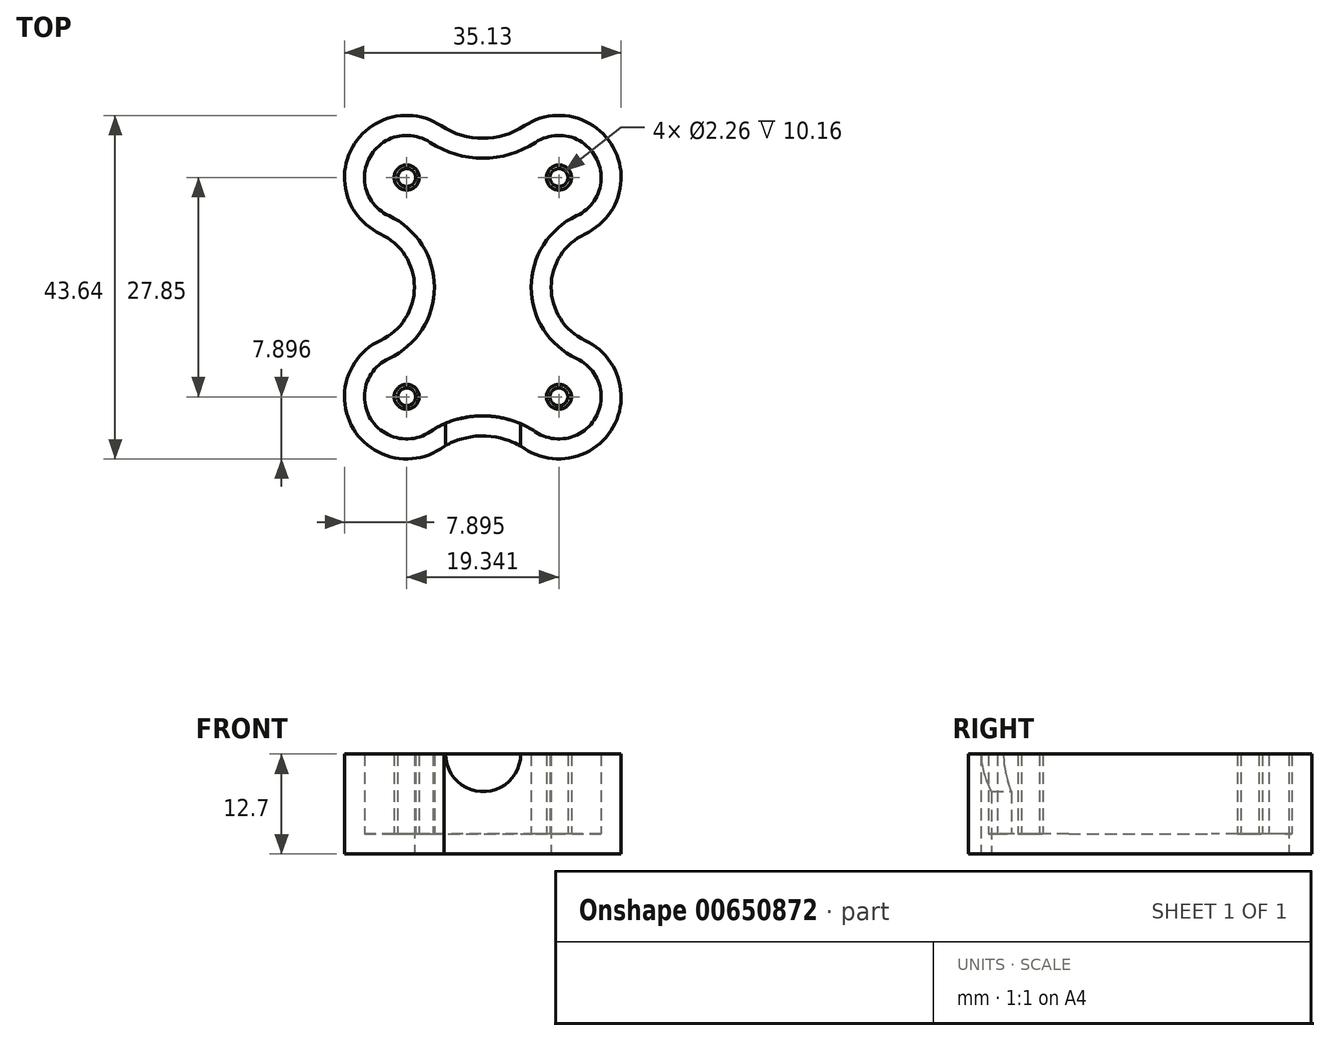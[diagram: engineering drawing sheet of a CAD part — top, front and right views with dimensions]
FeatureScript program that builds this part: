
annotation { "Feature Type Name" : "Feature", "Feature Type Description" : "" }
export const myFeature = defineFeature(function(context is Context, id is Id, definition is map)
    precondition{}
    {
        {
            var Q0;
            Q0=qCreatedBy(makeId("Top.planeOp"),FACE);
            var sketch = newSketch(context, id + "F0", { "sketchPlane" : qUnion([Q0])});
            skCircle(sketch, "E0", {"center": v(-19.03, 22.87) * mm, "radius": 7.9 * mm});
            skCircle(sketch, "E1", {"center": v(0.3, 22.87) * mm, "radius": 7.9 * mm});
            skCircle(sketch, "E2", {"center": v(-19.03, -4.98) * mm, "radius": 7.9 * mm});
            skCircle(sketch, "E3", {"center": v(0.3, -4.98) * mm, "radius": 7.9 * mm});
            skArc(sketch, "E4", {"start": v(-14.68, 29.45) * mm, "mid": v(-9.36, 27.85) * mm, "end": v(-4.05, 29.45) * mm});
            skArc(sketch, "E5", {"start": v(3.63, 15.7) * mm, "mid": v(-0.68, 8.94) * mm, "end": v(3.63, 2.18) * mm});
            skArc(sketch, "E6", {"start": v(-22.36, 2.18) * mm, "mid": v(-18.05, 8.94) * mm, "end": v(-22.36, 15.7) * mm});
            skArc(sketch, "E7", {"start": v(-4.06, -11.56) * mm, "mid": v(-9.13, -9.96) * mm, "end": v(-14.28, -11.29) * mm});
            skSolve(sketch);
        }
        {
            var Q0;
            {var subQ3=sQuery(id+"F0.wireOp",EDGE,"E4");Q0=makeQuery(id+"F0.imprint","IMPRINT",FACE,{"disambiguationData":[TD([[makeQuery(id+"F0.imprint","IMPRINT",EDGE,{"derivedFrom":subQ3}),-1.0]])]});}
            var Q1;
            {var subQ0=sQuery(id+"F0.wireOp",EDGE,"E0");var subQ1=makeQuery(id+"F0.imprint","INTERSECT",VERTEX,{"derivedFrom":[subQ0,sQuery(id+"F0.wireOp",EDGE,"E4")]});Q1=makeQuery(id+"F0.imprint","IMPRINT",FACE,{"disambiguationData":[TD([[makeQuery(id+"F0.imprint","IMPRINT",EDGE,{"disambiguationData":[TD([[subQ1,-1.0]])],"derivedFrom":subQ0}),1.0]])]});}
            var Q2;
            {var subQ0=sQuery(id+"F0.wireOp",EDGE,"E1");var subQ1=makeQuery(id+"F0.imprint","INTERSECT",VERTEX,{"derivedFrom":[subQ0,sQuery(id+"F0.wireOp",EDGE,"E4")]});Q2=makeQuery(id+"F0.imprint","IMPRINT",FACE,{"disambiguationData":[TD([[makeQuery(id+"F0.imprint","IMPRINT",EDGE,{"disambiguationData":[TD([[subQ1,-1.0]])],"derivedFrom":subQ0}),1.0]])]});}
            var Q3;
            {var subQ0=sQuery(id+"F0.wireOp",EDGE,"E2");var subQ1=makeQuery(id+"F0.imprint","INTERSECT",VERTEX,{"derivedFrom":[subQ0,sQuery(id+"F0.wireOp",EDGE,"E6")]});Q3=makeQuery(id+"F0.imprint","IMPRINT",FACE,{"disambiguationData":[TD([[makeQuery(id+"F0.imprint","IMPRINT",EDGE,{"disambiguationData":[TD([[subQ1,-1.0]])],"derivedFrom":subQ0}),1.0]])]});}
            var Q4;
            {var subQ0=sQuery(id+"F0.wireOp",EDGE,"E3");var subQ1=makeQuery(id+"F0.imprint","INTERSECT",VERTEX,{"derivedFrom":[subQ0,sQuery(id+"F0.wireOp",EDGE,"E5")]});Q4=makeQuery(id+"F0.imprint","IMPRINT",FACE,{"disambiguationData":[TD([[makeQuery(id+"F0.imprint","IMPRINT",EDGE,{"disambiguationData":[TD([[subQ1,-1.0]])],"derivedFrom":subQ0}),1.0]])]});}
            extrude(context, id + "F1", {"entities" : qUnion([Q0, Q1, Q2, Q3, Q4]), "depth" : 12.7 * mm, "offsetDistance" : 25.4 * mm});
        }
        {
            var Q0;
            Q0=makeQuery(id+"F1.opExtrude","CAP_FACE",FACE,{"disambiguationData":[OSD([sQuery(id+"F0.wireOp",EDGE,"E0"),sQuery(id+"F0.wireOp",EDGE,"E1"),sQuery(id+"F0.wireOp",EDGE,"E2"),sQuery(id+"F0.wireOp",EDGE,"E3"),sQuery(id+"F0.wireOp",EDGE,"E4"),sQuery(id+"F0.wireOp",EDGE,"E5"),sQuery(id+"F0.wireOp",EDGE,"E6"),sQuery(id+"F0.wireOp",EDGE,"E7")])],"isStart":false});
            shell(context, id + "F2", {"entities" : qUnion([Q0]), "thickness" : 2.54 * mm});
        }
        {
            var Q0;
            Q0=makeQuery(id+"F2.opShell","OFFSET_FACE",FACE,{"disambiguationData":[OSD([sQuery(id+"F0.wireOp",EDGE,"E0"),sQuery(id+"F0.wireOp",EDGE,"E1"),sQuery(id+"F0.wireOp",EDGE,"E2"),sQuery(id+"F0.wireOp",EDGE,"E3"),sQuery(id+"F0.wireOp",EDGE,"E4"),sQuery(id+"F0.wireOp",EDGE,"E5"),sQuery(id+"F0.wireOp",EDGE,"E6"),sQuery(id+"F0.wireOp",EDGE,"E7")])]});
            var sketch = newSketch(context, id + "F3", { "sketchPlane" : qUnion([Q0])});
            skCircle(sketch, "E8", {"center": v(-19.03, 22.87) * mm, "radius": 1.59 * mm});
            skCircle(sketch, "E9", {"center": v(0.3, 22.87) * mm, "radius": 1.59 * mm});
            skCircle(sketch, "E10", {"center": v(-19.03, -4.98) * mm, "radius": 1.59 * mm});
            skCircle(sketch, "E11", {"center": v(0.3, -4.98) * mm, "radius": 1.59 * mm});
            skSolve(sketch);
        }
        {
            var Q0;
            Q0=makeQuery(id+"F3.imprint","IMPRINT",FACE,{"disambiguationData":[TD([[makeQuery(id+"F3.imprint","IMPRINT",EDGE,{"derivedFrom":sQuery(id+"F3.wireOp",EDGE,"E8")}),1.0]])]});
            var Q1;
            Q1=makeQuery(id+"F3.imprint","IMPRINT",FACE,{"disambiguationData":[TD([[makeQuery(id+"F3.imprint","IMPRINT",EDGE,{"derivedFrom":sQuery(id+"F3.wireOp",EDGE,"E9")}),1.0]])]});
            var Q2;
            Q2=makeQuery(id+"F3.imprint","IMPRINT",FACE,{"disambiguationData":[TD([[makeQuery(id+"F3.imprint","IMPRINT",EDGE,{"derivedFrom":sQuery(id+"F3.wireOp",EDGE,"E10")}),1.0]])]});
            var Q3;
            Q3=makeQuery(id+"F3.imprint","IMPRINT",FACE,{"disambiguationData":[TD([[makeQuery(id+"F3.imprint","IMPRINT",EDGE,{"derivedFrom":sQuery(id+"F3.wireOp",EDGE,"E11")}),1.0]])]});
            var Q4;
            Q4=sQuery(id+"F3.wireOp",EDGE,"E8");
            var Q5;
            Q5=makeQuery(id+"F1.opExtrude","CAP_FACE",FACE,{"disambiguationData":[OSD([sQuery(id+"F0.wireOp",EDGE,"E0"),sQuery(id+"F0.wireOp",EDGE,"E1"),sQuery(id+"F0.wireOp",EDGE,"E2"),sQuery(id+"F0.wireOp",EDGE,"E3"),sQuery(id+"F0.wireOp",EDGE,"E4"),sQuery(id+"F0.wireOp",EDGE,"E5"),sQuery(id+"F0.wireOp",EDGE,"E6"),sQuery(id+"F0.wireOp",EDGE,"E7")])],"isStart":false});
            extrude(context, id + "F4", {"entities" : qUnion([Q0, Q1, Q2, Q3]), "operationType" : NewBodyOperationType.ADD, "surfaceEntities" : qUnion([Q4]), "endBound" : BoundingType.UP_TO_SURFACE, "depth" : 25.4 * mm, "endBoundEntityFace" : qUnion([Q5]), "offsetDistance" : 25.4 * mm});
        }
        {
            var Q0;
            Q0=sQuery(id+"F3.wireOp",VERTEX,"E8.center");
            var Q1;
            Q1=makeQuery(id+"F1.opExtrude","SWEPT_BODY",BODY,{"disambiguationData":[OSD([sQuery(id+"F0.wireOp",EDGE,"E0"),sQuery(id+"F0.wireOp",EDGE,"E1"),sQuery(id+"F0.wireOp",EDGE,"E2"),sQuery(id+"F0.wireOp",EDGE,"E3"),sQuery(id+"F0.wireOp",EDGE,"E4"),sQuery(id+"F0.wireOp",EDGE,"E5"),sQuery(id+"F0.wireOp",EDGE,"E6"),sQuery(id+"F0.wireOp",EDGE,"E7")])]});
            hole(context, id + "F5", {"style" : HoleStyle.SIMPLE, "endStyle" : HoleEndStyle.THROUGH, "oppositeDirection" : true, "standardTappedOrClearance" : lookupTablePath({ "standard" : "ANSI", "fit" : "Close", "size" : "#2", "type" : "Clearance" }), "standardBlindInLast" : lookupTablePath({ "fit" : "Close", "standard" : "ANSI", "size" : "#2", "type" : "Clearance" }), "holeDiameter" : 2.26 * mm, "majorDiameter" : 3 * mm, "isTappedThrough" : true, "tappedDepth" : 12.7 * mm, "tapClearance" : 3, "startFromSketch" : true, "locations" : qUnion([Q0]), "scope" : qUnion([Q1])});
        }
        {
            var Q0;
            Q0=sQuery(id+"F3.wireOp",VERTEX,"E9.center");
            var Q1;
            Q1=sQuery(id+"F3.wireOp",VERTEX,"E11.center");
            var Q2;
            Q2=sQuery(id+"F3.wireOp",VERTEX,"E10.center");
            var Q3;
            Q3=makeQuery(id+"F1.opExtrude","SWEPT_BODY",BODY,{"disambiguationData":[OSD([sQuery(id+"F0.wireOp",EDGE,"E0"),sQuery(id+"F0.wireOp",EDGE,"E1"),sQuery(id+"F0.wireOp",EDGE,"E2"),sQuery(id+"F0.wireOp",EDGE,"E3"),sQuery(id+"F0.wireOp",EDGE,"E4"),sQuery(id+"F0.wireOp",EDGE,"E5"),sQuery(id+"F0.wireOp",EDGE,"E6"),sQuery(id+"F0.wireOp",EDGE,"E7")])]});
            hole(context, id + "F6", {"style" : HoleStyle.SIMPLE, "endStyle" : HoleEndStyle.THROUGH, "oppositeDirection" : true, "standardTappedOrClearance" : lookupTablePath({ "standard" : "ANSI", "fit" : "Close", "size" : "#2", "type" : "Clearance" }), "standardBlindInLast" : lookupTablePath({ "fit" : "Close", "standard" : "ANSI", "size" : "#2", "type" : "Clearance" }), "holeDiameter" : 2.26 * mm, "majorDiameter" : 6.35 * mm, "isTappedThrough" : true, "tappedDepth" : 12.7 * mm, "tapClearance" : 3, "startFromSketch" : true, "locations" : qUnion([Q0, Q1, Q2]), "scope" : qUnion([Q3])});
        }
        {
            var Q0;
            Q0=qCreatedBy(makeId("Front.planeOp"),FACE);
            var sketch = newSketch(context, id + "F7", { "sketchPlane" : qUnion([Q0])});
            skCircle(sketch, "E12", {"center": v(-9.31, 12.7) * mm, "radius": 4.76 * mm});
            skSolve(sketch);
        }
        {
            var Q0;
            Q0 = qSketchRegion(id + "F7", true);
            extrude(context, id + "F8", {"entities" : qUnion([Q0]), "operationType" : NewBodyOperationType.REMOVE, "depth" : 25.4 * mm, "offsetDistance" : 25.4 * mm});
        }
    });
